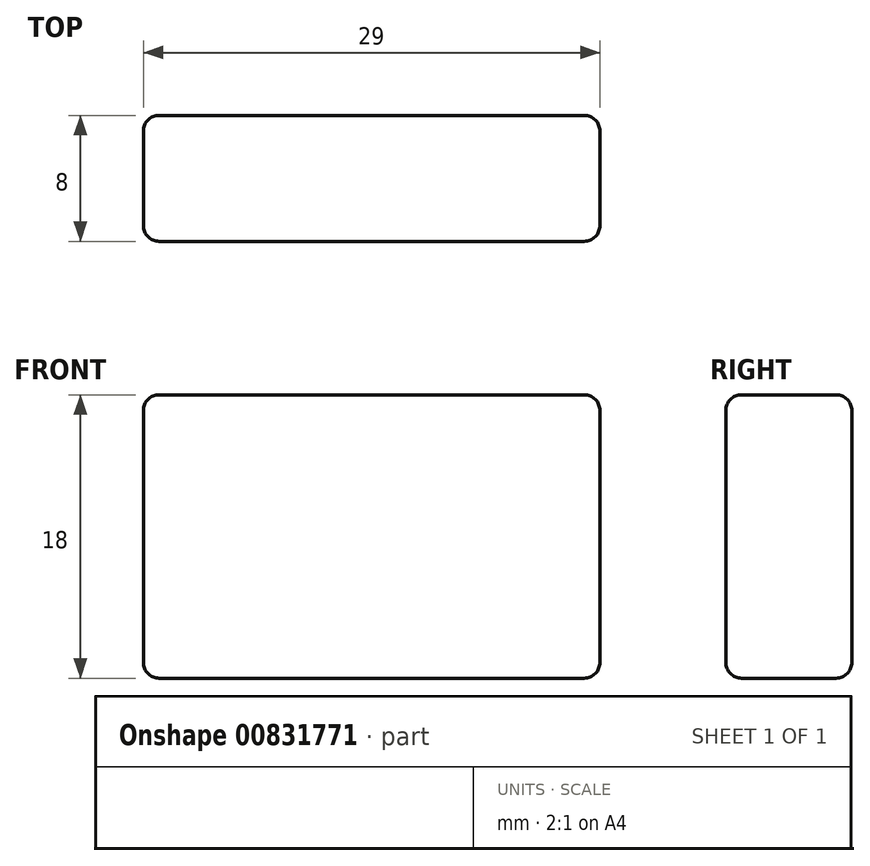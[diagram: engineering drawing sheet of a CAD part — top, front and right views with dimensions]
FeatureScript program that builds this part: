
annotation { "Feature Type Name" : "Feature", "Feature Type Description" : "" }
export const myFeature = defineFeature(function(context is Context, id is Id, definition is map)
    precondition{}
    {
        {
            var Q0;
            Q0=qCreatedBy(makeId("Front.planeOp"),FACE);
            var sketch = newSketch(context, id + "F0", { "sketchPlane" : qUnion([Q0])});
            skLineSegment(sketch, "E0.bottom", {"start": v(0, 0) * mm, "end": v(29, 0) * mm});
            skLineSegment(sketch, "E0.top", {"start": v(0, 18) * mm, "end": v(29, 18) * mm});
            skLineSegment(sketch, "E0.left", {"start": v(0, 0) * mm, "end": v(0, 18) * mm});
            skLineSegment(sketch, "E0.right", {"start": v(29, 0) * mm, "end": v(29, 18) * mm});
            skSolve(sketch);
        }
        {
            var Q0;
            Q0=makeQuery(id+"F0.imprint","IMPRINT",FACE,{"disambiguationData":[TD([[makeQuery(id+"F0.imprint","IMPRINT",EDGE,{"derivedFrom":sQuery(id+"F0.wireOp",EDGE,"E0.bottom")}),1.0]])]});
            extrude(context, id + "F1", {"entities" : qUnion([Q0]), "depth" : 8 * mm, "offsetDistance" : 25 * mm});
        }
        {
            var Q0;
            Q0=makeQuery(id+"F1.opExtrude","CAP_EDGE",EDGE,{"disambiguationData":[OSD([sQuery(id+"F0.wireOp",EDGE,"E0.bottom")])],"isStart":false});
            var Q1;
            Q1=makeQuery(id+"F1.opExtrude","CAP_EDGE",EDGE,{"disambiguationData":[OSD([sQuery(id+"F0.wireOp",EDGE,"E0.left")])],"isStart":false});
            var Q2;
            Q2=makeQuery(id+"F1.opExtrude","CAP_EDGE",EDGE,{"disambiguationData":[OSD([sQuery(id+"F0.wireOp",EDGE,"E0.top")])],"isStart":false});
            var Q3;
            Q3=makeQuery(id+"F1.opExtrude","CAP_EDGE",EDGE,{"disambiguationData":[OSD([sQuery(id+"F0.wireOp",EDGE,"E0.right")])],"isStart":false});
            var Q4;
            Q4=makeQuery(id+"F1.opExtrude","SWEPT_EDGE",EDGE,{"disambiguationData":[OSD([sQuery(id+"F0.wireOp",EDGE,"E0.bottom"),sQuery(id+"F0.wireOp",EDGE,"E0.left")])]});
            var Q5;
            Q5=makeQuery(id+"F1.opExtrude","SWEPT_EDGE",EDGE,{"disambiguationData":[OSD([sQuery(id+"F0.wireOp",EDGE,"E0.top"),sQuery(id+"F0.wireOp",EDGE,"E0.right")])]});
            var Q6;
            Q6=makeQuery(id+"F1.opExtrude","SWEPT_EDGE",EDGE,{"disambiguationData":[OSD([sQuery(id+"F0.wireOp",EDGE,"E0.bottom"),sQuery(id+"F0.wireOp",EDGE,"E0.right")])]});
            var Q7;
            Q7=makeQuery(id+"F1.opExtrude","SWEPT_EDGE",EDGE,{"disambiguationData":[OSD([sQuery(id+"F0.wireOp",EDGE,"E0.top"),sQuery(id+"F0.wireOp",EDGE,"E0.left")])]});
            var Q8;
            Q8=makeQuery(id+"F1.opExtrude","CAP_EDGE",EDGE,{"disambiguationData":[OSD([sQuery(id+"F0.wireOp",EDGE,"E0.top")])],"isStart":true});
            var Q9;
            Q9=makeQuery(id+"F1.opExtrude","CAP_EDGE",EDGE,{"disambiguationData":[OSD([sQuery(id+"F0.wireOp",EDGE,"E0.left")])],"isStart":true});
            var Q10;
            Q10=makeQuery(id+"F1.opExtrude","CAP_EDGE",EDGE,{"disambiguationData":[OSD([sQuery(id+"F0.wireOp",EDGE,"E0.bottom")])],"isStart":true});
            var Q11;
            Q11=makeQuery(id+"F1.opExtrude","CAP_EDGE",EDGE,{"disambiguationData":[OSD([sQuery(id+"F0.wireOp",EDGE,"E0.right")])],"isStart":true});
            fillet(context, id + "F2", {"entities" : qUnion([Q0, Q1, Q2, Q3, Q4, Q5, Q6, Q7, Q8, Q9, Q10, Q11]), "radius" : 1 * mm, "tangentPropagation" : true, "allowEdgeOverflow" : false});
        }
    });
